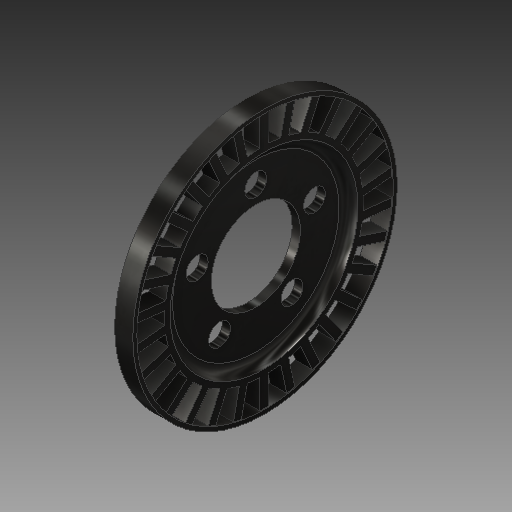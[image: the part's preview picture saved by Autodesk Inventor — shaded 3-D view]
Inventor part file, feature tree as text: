
AUTODESK INVENTOR PART (.ipt)
format: ipt  version: 2019 (Build 230136000, 136)  size: 336,896 bytes
history: native  units: mm
features: sketch x6, extrude x5, pattern_circular x2, plane x1, fillet x1
ambient origin geometry x8: Origin, YZ Plane, XZ Plane, XY Plane, X Axis, Y Axis, Z Axis, Center Point
bodies: Solid1 (feature_tree)
feature tree (15):
  extrude  "Extrusion1"  Depth=145.0mm
  extrude  "Extrusion2"  Depth=12.0mm
  plane  "Work Plane1"
  extrude  "Extrusion3"  Depth=0.5mm
  extrude  "Extrusion4"  Depth=187.0mm
  pattern_circular  "Circular Pattern1"  [2 undecoded]
  fillet  "Fillet3"  Radius=7.228mm
  extrude  "Extrusion5"  Depth=10.0mm TaperAngle=360.0deg
  pattern_circular  "Circular Pattern2"  [2 undecoded]
  sketch  "Sketch7"  dims[d26=6.0mm d27=22.0mm d28=7.228mm d29=0.0mm d30=300.0mm d31=360.0deg d36=8.0mm d37=90.0mm d40=16.0mm d41=10.0mm d42=0.0mm d43=50.0mm d44=360.0deg]
  sketch  "Sketch1"  dims[d1=65.0mm d2=145.0mm]
  sketch  "Sketch2"  dims[d15=12.0mm d16=0.0mm d17=137.0mm]
  sketch  "Sketch4"  dims[d18=6.0mm d19=0.0mm d20=0.5mm]
  sketch  "Sketch5"  dims[d21=193.0mm d22=187.0mm]
  sketch  "Sketch6"  dims[d23=13.228mm d24=0.0mm]
note: 4 required parameter values undecoded (feature->parameter linkage not recoverable at this tier; creation-order binding heuristic only, values carry confidence <= 0.55)
